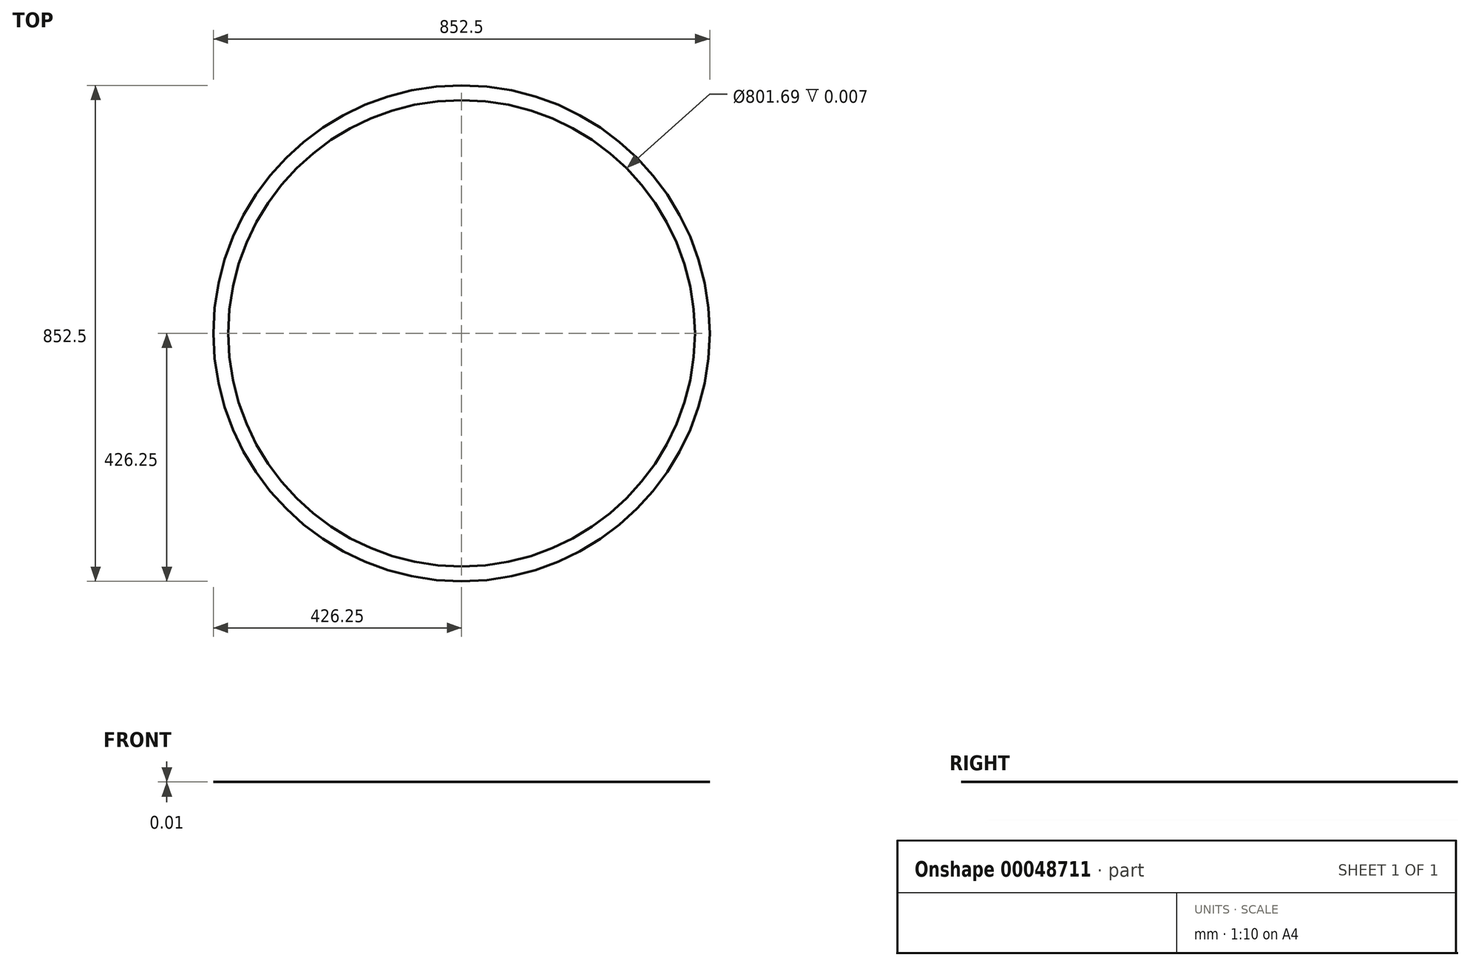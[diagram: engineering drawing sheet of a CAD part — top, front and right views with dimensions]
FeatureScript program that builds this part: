
annotation { "Feature Type Name" : "Feature", "Feature Type Description" : "" }
export const myFeature = defineFeature(function(context is Context, id is Id, definition is map)
    precondition{}
    {
        {
            var Q0;
            Q0=qCreatedBy(makeId("Top.planeOp"),FACE);
            var sketch = newSketch(context, id + "F0", { "sketchPlane" : qUnion([Q0])});
            skCircle(sketch, "E0", {"center": v(0, 0) * mm, "radius": 426.25 * mm});
            skCircle(sketch, "E1", {"center": v(0, 0) * mm, "radius": 400.85 * mm});
            skSolve(sketch);
        }
        {
            var Q0;
            Q0 = qSketchRegion(id + "F0", true);
            extrude(context, id + "F1", {"entities" : qUnion([Q0]), "depth" : 3 / 457.2 * mm});
        }
    });
